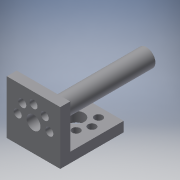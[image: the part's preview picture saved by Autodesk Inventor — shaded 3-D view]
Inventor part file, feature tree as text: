
AUTODESK INVENTOR PART (.ipt)
format: ipt  version: 2016 (Build 200138000, 138)  size: 155,136 bytes
history: native  units: mm
features: sketch x6, reference x5, extrude x3, hole x3
ambient origin geometry x8: Origin, YZ Plane, XZ Plane, XY Plane, X Axis, Y Axis, Z Axis, Center Point
bodies: Body1 (feature_tree)
feature tree (17):
  extrude  "Extrusion2"  Depth=27.0mm
  extrude  "Extrusion4"  Depth=5.0mm TaperAngle=0.0deg
  hole  "Hole1"  [1 undecoded]
  hole  "Hole2"  [1 undecoded]
  extrude  "Extrusion5"  Depth=27.0mm
  hole  "Hole3"  [1 undecoded]
  sketch  "Sketch1"  dims[d0=27.0mm d1=27.0mm]
  sketch  "Sketch4"  dims[d5=7.0mm d6=5.0mm d7=0.0mm]
  sketch  "Sketch5"  dims[d11=27.0mm d12=5.0mm]
  sketch  "Sketch7"  dims[d13=27.0mm d14=0.0mm d15=27.0mm]
  reference  "Reference2"
  reference  "Reference3"
  reference  "Reference4"
  reference  "Reference5"
  reference  "Reference6"
  sketch  "Sketch9"  dims[d16=27.0mm d17=8.0mm]
  sketch  "Sketch10"  dims[d18=8.0mm d19=6.0mm d20=4.0mm d21=2.0mm d22=90.0deg d23=5.0mm d24=20.594885mm d25=4.0mm d26=6.0mm d27=4.0mm d28=2.0mm d29=90.0deg d30=8.0mm d31=20.594885mm d33=9.0mm d34=52.0mm d35=0.0mm d36=4.0mm d37=6.0mm d38=4.0mm d39=2.0mm d40=90.0deg d41=5.0mm d42=20.594885mm]
note: 3 required parameter values undecoded (feature->parameter linkage not recoverable at this tier; creation-order binding heuristic only, values carry confidence <= 0.55)
